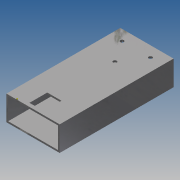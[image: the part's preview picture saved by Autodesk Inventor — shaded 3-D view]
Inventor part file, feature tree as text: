
AUTODESK INVENTOR PART (.ipt)
format: ipt  version: 2014 SP1 (Build 180222100, 222)  size: 174,080 bytes
history: native  units: in
note: dims shown in document units (in); Inventor stores cm internally (conversion verified against a paired STEP export)
features: sketch x10, extrude x7, hole x3
ambient origin geometry x8: Origin, YZ Plane, XZ Plane, XY Plane, X Axis, Y Axis, Z Axis, Center Point
bodies: Solid1 (feature_tree)
feature tree (20):
  extrude  "Extrusion1"  Depth=1.5in
  extrude  "Extrusion3"  Depth=8.0in TaperAngle=0.0deg
  extrude  "Extrusion4"  Depth=1.0in
  extrude  "Extrusion5"  Depth=0.5in TaperAngle=0.0deg
  extrude  "Extrusion6"  Depth=1.0in TaperAngle=0.0deg
  hole  "Hole1"  [1 undecoded]
  extrude  "Extrusion7"  Depth=0.1in
  extrude  "Extrusion8"  Depth=1.0in
  hole  "Hole3"  [1 undecoded]
  hole  "Hole4"  [1 undecoded]
  sketch  "Sketch1"  dims[d0=3.5in d1=1.5in]
  sketch  "Sketch3"  dims[d2=0.12in d3=8.0in d4=0.0in]
  sketch  "Sketch4"  dims[d10=0.1in d11=1.0in]
  sketch  "Sketch5"  dims[d12=0.6in d13=0.5in d14=0.0in]
  sketch  "Sketch6"  dims[d15=0.5in d16=1.0in d17=0.0in]
  sketch  "Sketch7"  dims[d18=1.0in d19=1.25in]
  sketch  "Sketch9"  dims[d20=1.75in d21=0.1in]
  sketch  "Sketch11"  dims[d22=0.5in d23=0.0in d24=1.0in]
  sketch  "Sketch12"  dims[d25=0.5in d26=0.5in d27=0.0in]
  sketch  "Sketch13"  dims[d28=0.2in d29=0.13in d30=3.0in d31=0.375in d32=0.25in d33=0.5635in d34=1.0in d35=0.8108in d54=0.05in d55=0.05in d56=0.05in d57=0.0in d58=0.005in d60=0.25in d61=1.25in d62=1.0in d63=0.5in d64=0.0in d65=0.25in d66=0.75in d67=0.87in d68=0.25in d70=2.0in d73=0.25in d74=0.75in d75=0.375in d76=0.25in d77=0.5635in d78=1.0in d79=0.8108in d80=1.5in d81=0.25in d82=0.75in d83=0.375in d84=0.25in d85=0.5635in d86=1.0in d87=0.8108in]
note: 3 required parameter values undecoded (feature->parameter linkage not recoverable at this tier; creation-order binding heuristic only, values carry confidence <= 0.55)
